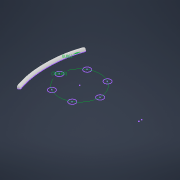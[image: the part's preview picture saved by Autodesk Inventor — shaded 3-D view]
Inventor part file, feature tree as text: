
AUTODESK INVENTOR PART (.ipt)
format: ipt  version: 2022 (Build 260153000, 153)  size: 201,728 bytes
history: native  units: mm
features: sketch x3, fillet x2, extrude x1, hole x1
ambient origin geometry x8: Origin, YZ Plane, XZ Plane, XY Plane, X Axis, Y Axis, Z Axis, Center Point
bodies: Solid1 (feature_tree)
feature tree (7):
  sketch  "Sketch2"  dims[d1=60.0mm d5=360.0deg d24=4.5mm d25=0.0mm d26=2.498mm]
  extrude  "Extrusion1"  Depth=2.498mm TaperAngle=0.0deg
  fillet  "Fillet1"  Radius=2.498mm
  sketch  "Sketch3"  dims[d28=8.061767mm]
  sketch  "Sketch5"  dims[d31=4.8mm d32=6.0mm d33=4.0mm d34=2.0mm d35=90.0deg d36=2.5mm d37=0.0mm d38=2.4mm d39=1.0mm d40=1.0mm d41=1.0mm d42=0.15mm d43=0.25mm d44=0.375mm d45=14.3117mm d46=0.75mm d47=20.594885mm d48=0.0625mm d49=0.75mm d50=0.375mm]
  hole  "Hole1"  [1 undecoded]
  fillet  "Fillet2"  Radius=1.0mm
note: 1 required parameter value undecoded (feature->parameter linkage not recoverable at this tier; creation-order binding heuristic only, values carry confidence <= 0.55)
